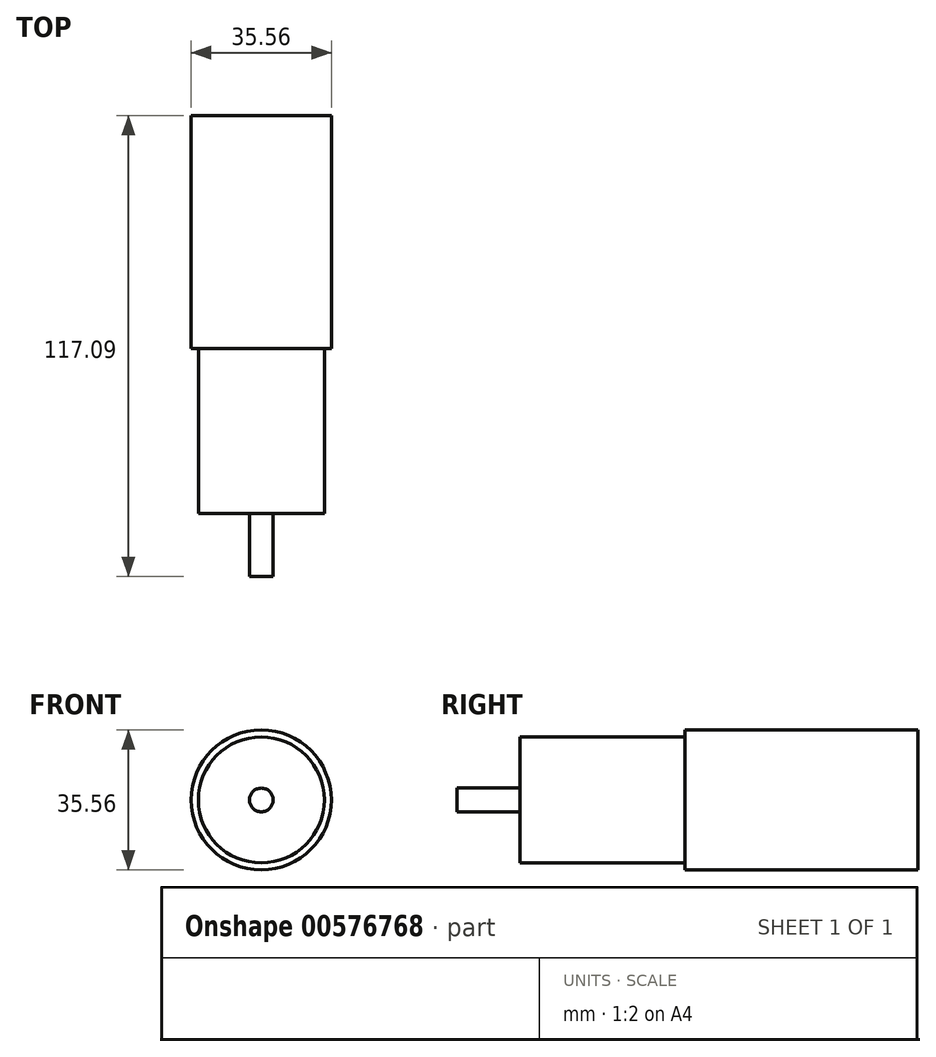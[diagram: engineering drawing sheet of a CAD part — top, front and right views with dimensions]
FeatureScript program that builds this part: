
annotation { "Feature Type Name" : "Feature", "Feature Type Description" : "" }
export const myFeature = defineFeature(function(context is Context, id is Id, definition is map)
    precondition{}
    {
        {
            var Q0;
            Q0=qCreatedBy(makeId("Front.planeOp"),FACE);
            var sketch = newSketch(context, id + "F0", { "sketchPlane" : qUnion([Q0])});
            skCircle(sketch, "E0", {"center": v(0, 0) * mm, "radius": 17.78 * mm});
            skSolve(sketch);
        }
        {
            var Q0;
            Q0 = qSketchRegion(id + "F0", true);
            extrude(context, id + "F1", {"entities" : qUnion([Q0]), "depth" : 59.18 * mm, "offsetDistance" : 25.4 * mm});
        }
        {
            var Q0;
            Q0=makeQuery(id+"F1.opExtrude","CAP_FACE",FACE,{"disambiguationData":[OSD([sQuery(id+"F0.wireOp",EDGE,"E0")])],"isStart":false});
            var sketch = newSketch(context, id + "F2", { "sketchPlane" : qUnion([Q0])});
            skCircle(sketch, "E1", {"center": v(0, 0) * mm, "radius": 16 * mm});
            skSolve(sketch);
        }
        {
            var Q0;
            Q0 = qSketchRegion(id + "F2", true);
            extrude(context, id + "F3", {"entities" : qUnion([Q0]), "operationType" : NewBodyOperationType.ADD, "depth" : 41.9 * mm, "offsetDistance" : 25.4 * mm});
        }
        {
            var Q0;
            Q0=makeQuery(id+"F3.opExtrude","CAP_FACE",FACE,{"disambiguationData":[OSD([sQuery(id+"F2.wireOp",EDGE,"E1")])],"isStart":false});
            var sketch = newSketch(context, id + "F4", { "sketchPlane" : qUnion([Q0])});
            skCircle(sketch, "E2", {"center": v(0, 0) * mm, "radius": 3 * mm});
            skSolve(sketch);
        }
        {
            var Q0;
            Q0=makeQuery(id+"F4.imprint","IMPRINT",FACE,{"disambiguationData":[TD([[makeQuery(id+"F4.imprint","IMPRINT",EDGE,{"derivedFrom":sQuery(id+"F4.wireOp",EDGE,"E2")}),1.0]])]});
            extrude(context, id + "F5", {"entities" : qUnion([Q0]), "operationType" : NewBodyOperationType.ADD, "depth" : 16 * mm, "offsetDistance" : 25.4 * mm});
        }
    });
